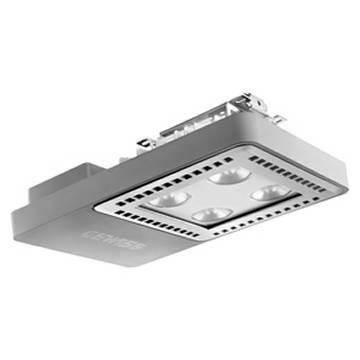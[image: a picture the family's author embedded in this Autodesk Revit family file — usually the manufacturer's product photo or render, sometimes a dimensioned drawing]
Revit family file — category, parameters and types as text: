
# Revit family: Lighting-Industriale-GEWISS-SMART[4]HLO_APPARECCHI-LED_1M
name_source: partatom
category: Apparecchi per illuminazione
units: mm (PartAtom-declared; Revit-internal decimal feet)

## family parameters
Basato su piano di lavoro = Sì
Condiviso = No
Numero OmniClass = 23.80.00.00
Punto di calcolo locali = No
Quota connettore circolare = Usa diametro
Sempre verticale = No
Sorgente d'illuminazione = No
Taglio con vuoti quando caricato = No
Tipo di parte = Normale
Titolo OmniClass = Electric Power and Lighting

## types (1)
- Lighting-Industriale-GEWISS-SMART[4]HLO_APPARECCHI-LED_1M
    Alimentatore = Incluso
    Apparecchio a ridotta temperatura superficiale = Si
    Applicazione = Interno
    Cablaggio = Con connettore stagno Gw connect
    Caratteristiche elettriche e gestione della luce = -
    Caratteristiche ottiche e illuminotecniche = -
    Carico apparente = 50 VA
    Catalogo = LIGHTING
    Certificazione DIN 18032-3 = Con Staffa - Kit Funi + morsetto (in approvazione)
    Certificazioni e classificazioni = -
    Classe fotobiologica = RG0
    Classe isolamento = I
    Classificazione = Lighting
    Classificazione: = -
    Codice Electrocod = 2444
    Codice digitale univoco (Datamatrix) = Datamatrix
    Colore = Grigio RAL 7035
    Commenti sul wattaggio = 50W
    Contesto = Illuminazione di logistiche e locali produttivi industriali
    Controllo abbagliamento e luminanza = -
    Corpo = PA6 “Halogen Free” caricato fibra vetro
    Descrizione = SMART[4]LB 1M C.PAS.ON/OFF HLO ELL.57K
    Dispositivo di protezione = DM 6kV / CM 6kV
    Distanza tot_plafoniera = 74 mm  [stored 0.242782 ft]
    Durata di vita = L90B10 (Tq+25°C) = 70.000 h - L90B10 (Tq+50°C) = 35.000 h
    Efficienza luminosa (lm/W) = 128
    Finitura colore = Grigio RAL 7035
    Fissaggio = -
    Frequenza nominale (Hz) = 50/60 Hz
    Gancio di chiusura = -
    Garanzia = 5 anni
    Grado di protezione = IP66
    Gruppo ottico = Riflettore in PC metallizzato e lenti in PMMA
    Guarnizioni = tipo siliconico antinvecchiamento
    IDF = 5e5a1ad8-9921-4241-a109-0c80e9b8793f
    IDT = 38a7e34fee1a4d0d9e54b5fc2166bea5
    IPEA = -
    Immagine tipo = GWL1071.jpg
    Inclinazione = Con accessorio staffa
    Indice di resa cromatica = CRI-80
    Informazioni generali = -
    Installazione e manutenzione = -
    Lampada = LED
    Larghezza = 253 mm  [stored 0.830052 ft]
    Lumen output (lm) = 8200
    Lunghezza = 383 mm  [stored 1.25656 ft]
    Materiali = -
    Modello = GWS4122BQ857
    Motore = <Per categoria>
    Norma di riferimento = EN 60598-1 ; EN 60598-2-1 ; EN 60598-2-24
    Ottica = Ellittica
    Peso (kg): = 3,5
    Plafoniera = <Per categoria>
    Potenza di sistema = 64W
    Produttore = GEWISS S.p.A.
    Prospetto di default = 1219 mm
    Raggio led = 30 mm  [stored 0.0984252 ft]
    Resistenza agli urti = IK08
    Resistenza al filo incandescente = 850 °C
    SEO = Low Bay
    Scheda Tecnica = https://www.gewiss.com
    Schermo = Vetro Temprato Spessore 4mm
    Sistema di controllo = ON / OFF
    Sistema di controllo : = ON / OFF
    Sostituibilità gruppo ottico = Non sostituibile
    Sostituibilità piastra di cablaggio = Non sostituibile
    Spessore plafoniera = 40 mm  [stored 0.131234 ft]
    Superficie massima esposta al vento : = 0,097 m²
    Temperatura di colore = 5700K
    Temperatura di esercizio = -30°C ÷ +50 °C
    Temperatura di stoccaggio = -40 +70 °C
    Tensione di alimentazione = 220 - 240 V
    Tipo di apparecchio = Riflettore industriale a LED&nbsp;
    Tipo di installazione e montaggio = Plafone - Parete - Sospensione
    Tipologia sorgente luminosa = LED - Non sostituibile
    Tolleranza cromatica = SDCM = 3
    Trasformatore = <Per categoria>
    URL = https://www.gewiss.com
    Vano di alimentazione = Integrato
    Versione file RFA = 20.11
    Vetro acceso = Lampada accesa
    Viti esterne = Acciaio inox
    Voltaggio = 230 V

note: [stored X ft] marks values corroborated as IEEE doubles in the binary element streams (Revit-internal decimal feet)

## geometry (parser evidence)
native form markers: Blend x4
no freeform markers — native parametric forms only
